# Revit family: Verano_V745_Luderitz_GM_R21
name_source: partatom
category: Generic Models
units: mm (PartAtom-declared; Revit-internal decimal feet)

## family parameters
Always vertical = Yes
Can host rebar = No
Cut with Voids When Loaded = No
Part Type = Normal
Room Calculation Point = No
Round Connector Dimension = Use Diameter
Shared = No
Work Plane-Based = No

## types (2) — shared parameters
Fixed Glass Bottom Offset = 78 mm
Fixed Glass Top Offset = 67 mm
Frame Material = V_Antracite
Glass Material = Glass
Manufacturer = Verano Systems
Maximal Height = 2500 mm  [stored 8.2021 ft]
Maximal Width = 3000 mm  [stored 9.84252 ft]
Minimal Height = 1500 mm  [stored 4.92126 ft]
Minimal Width = 1000 mm  [stored 3.28084 ft]
Model = V745 Luderitz
zero-valued in all types: Default Elevation

## per-type parameters (varying)
| type | Description | Glass_Slide_In | Glass_Slide_Out | URL |
| Glass Slide In |  | Yes | No |  |
| Glass Slide Out | Movable part elektrical operated | No | Yes | https://verano.nl |

note: [stored X ft] marks values corroborated as IEEE doubles in the binary element streams (Revit-internal decimal feet)

## geometry (parser evidence)
native form markers: Sweep x23
no freeform markers — native parametric forms only
